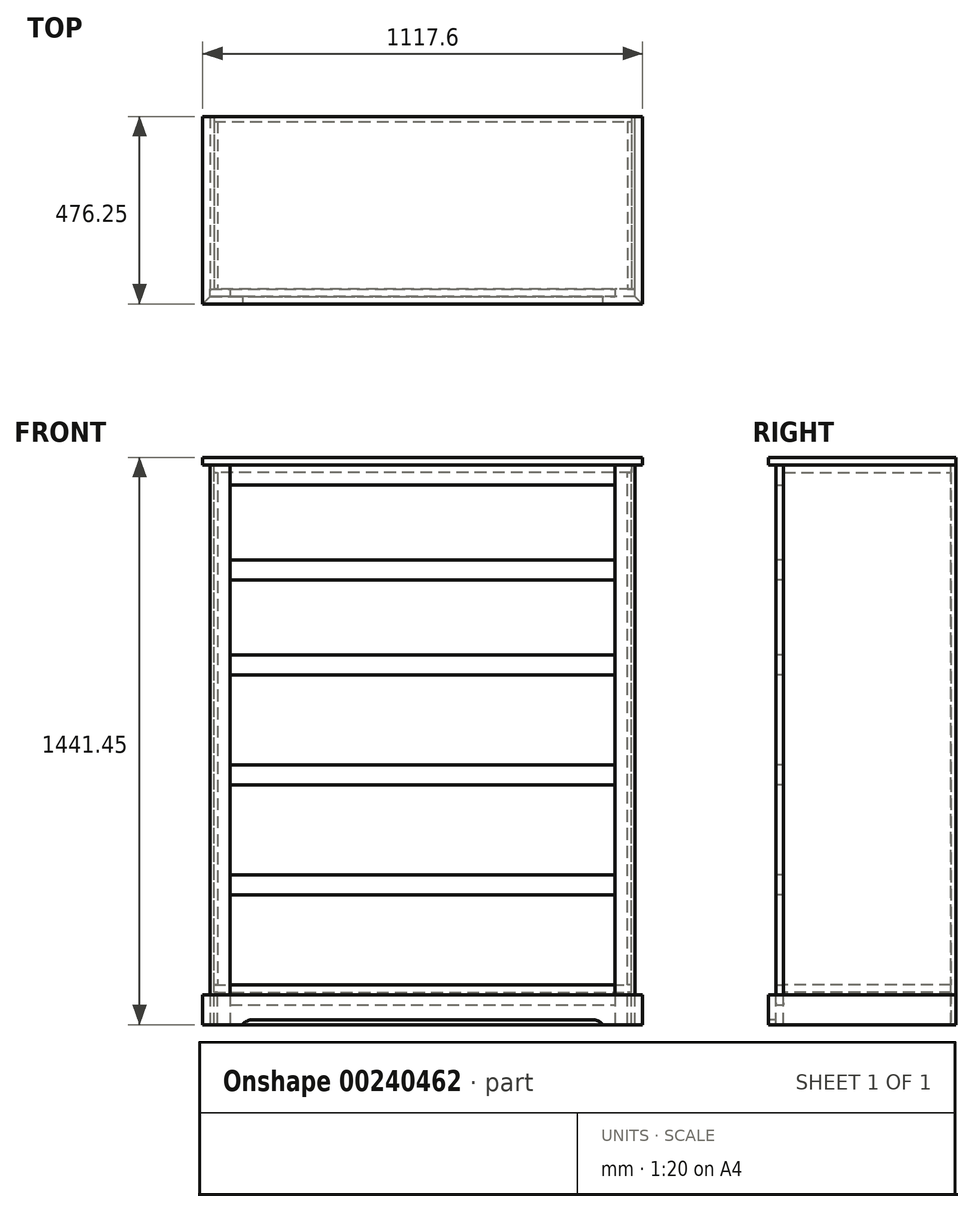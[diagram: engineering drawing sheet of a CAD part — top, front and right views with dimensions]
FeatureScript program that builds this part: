
annotation { "Feature Type Name" : "Feature", "Feature Type Description" : "" }
export const myFeature = defineFeature(function(context is Context, id is Id, definition is map)
    precondition{}
    {
        {
            var Q0;
            Q0=qCreatedBy(makeId("Right.planeOp"),FACE);
            var sketch = newSketch(context, id + "F0", { "sketchPlane" : qUnion([Q0])});
            skLineSegment(sketch, "E0.bottom", {"start": v(0, 0) * mm, "end": v(438.15, 0) * mm});
            skLineSegment(sketch, "E0.top", {"start": v(0, 1422.4) * mm, "end": v(438.15, 1422.4) * mm});
            skLineSegment(sketch, "E0.left", {"start": v(0, 0) * mm, "end": v(0, 1422.4) * mm});
            skLineSegment(sketch, "E0.right", {"start": v(438.15, 0) * mm, "end": v(438.15, 1422.4) * mm});
            skSolve(sketch);
        }
        {
            var Q0;
            Q0 = qSketchRegion(id + "F0", true);
            extrude(context, id + "F1", {"entities" : qUnion([Q0]), "oppositeDirection" : true, "depth" : 19.05 * mm});
        }
        {
            var Q0;
            Q0=makeQuery(id+"F1.opExtrude","SWEPT_FACE",FACE,{"disambiguationData":[OSD([sQuery(id+"F0.wireOp",EDGE,"E0.left")])]});
            var sketch = newSketch(context, id + "F2", { "sketchPlane" : qUnion([Q0])});
            skLineSegment(sketch, "E1.bottom", {"start": v(-9.52, 82.55) * mm, "end": v(-1069.98, 82.55) * mm});
            skLineSegment(sketch, "E1.top", {"start": v(-9.52, 101.6) * mm, "end": v(-1069.98, 101.6) * mm});
            skLineSegment(sketch, "E1.left", {"start": v(-9.52, 82.55) * mm, "end": v(-9.52, 101.6) * mm});
            skLineSegment(sketch, "E1.right", {"start": v(-1069.98, 82.55) * mm, "end": v(-1069.98, 101.6) * mm});
            skSolve(sketch);
        }
        {
            var Q0;
            Q0 = qSketchRegion(id + "F2", true);
            extrude(context, id + "F3", {"entities" : qUnion([Q0]), "oppositeDirection" : true, "depth" : 438.15 * mm});
        }
        {
            var Q0;
            Q0=makeQuery(id+"F3.opExtrude","SWEPT_BODY",BODY,{"disambiguationData":[OSD([sQuery(id+"F2.wireOp",EDGE,"E1.bottom"),sQuery(id+"F2.wireOp",EDGE,"E1.top"),sQuery(id+"F2.wireOp",EDGE,"E1.left"),sQuery(id+"F2.wireOp",EDGE,"E1.right")])]});
            var Q1;
            Q1=makeQuery(id+"F1.opExtrude","SWEPT_BODY",BODY,{"disambiguationData":[OSD([sQuery(id+"F0.wireOp",EDGE,"E0.bottom"),sQuery(id+"F0.wireOp",EDGE,"E0.top"),sQuery(id+"F0.wireOp",EDGE,"E0.left"),sQuery(id+"F0.wireOp",EDGE,"E0.right")])]});
            booleanBodies(context, id + "F4", {"operationType" : BooleanOperationType.SUBTRACTION, "tools" : qUnion([Q0]), "targets" : qUnion([Q1]), "keepTools" : true});
        }
        {
            var Q0;
            Q0=makeQuery(id+"F3.opExtrude","CAP_FACE",FACE,{"disambiguationData":[OSD([sQuery(id+"F2.wireOp",EDGE,"E1.bottom"),sQuery(id+"F2.wireOp",EDGE,"E1.top"),sQuery(id+"F2.wireOp",EDGE,"E1.left"),sQuery(id+"F2.wireOp",EDGE,"E1.right")])],"isStart":true});
            var sketch = newSketch(context, id + "F5", { "sketchPlane" : qUnion([Q0])});
            skLineSegment(sketch, "E2.bottom", {"start": v(-1079.5, 1422.4) * mm, "end": v(-1060.45, 1422.4) * mm});
            skLineSegment(sketch, "E2.top", {"start": v(-1079.5, 0) * mm, "end": v(-1060.45, 0) * mm});
            skLineSegment(sketch, "E2.left", {"start": v(-1079.5, 1422.4) * mm, "end": v(-1079.5, 0) * mm});
            skLineSegment(sketch, "E2.right", {"start": v(-1060.45, 1422.4) * mm, "end": v(-1060.45, 0) * mm});
            skSolve(sketch);
        }
        {
            var Q0;
            Q0 = qSketchRegion(id + "F5", true);
            extrude(context, id + "F6", {"entities" : qUnion([Q0]), "oppositeDirection" : true, "depth" : 438.15 * mm});
        }
        {
            var Q0;
            Q0=makeQuery(id+"F3.opExtrude","SWEPT_BODY",BODY,{"disambiguationData":[OSD([sQuery(id+"F2.wireOp",EDGE,"E1.bottom"),sQuery(id+"F2.wireOp",EDGE,"E1.top"),sQuery(id+"F2.wireOp",EDGE,"E1.left"),sQuery(id+"F2.wireOp",EDGE,"E1.right")])]});
            var Q1;
            Q1=makeQuery(id+"F6.opExtrude","SWEPT_BODY",BODY,{"disambiguationData":[OSD([sQuery(id+"F5.wireOp",EDGE,"E2.bottom"),sQuery(id+"F5.wireOp",EDGE,"E2.top"),sQuery(id+"F5.wireOp",EDGE,"E2.left"),sQuery(id+"F5.wireOp",EDGE,"E2.right")])]});
            booleanBodies(context, id + "F7", {"operationType" : BooleanOperationType.SUBTRACTION, "tools" : qUnion([Q0]), "targets" : qUnion([Q1]), "keepTools" : true});
        }
        {
            var Q0;
            Q0=makeQuery(id+"F6.opExtrude","CAP_FACE",FACE,{"disambiguationData":[OSD([sQuery(id+"F5.wireOp",EDGE,"E2.bottom"),sQuery(id+"F5.wireOp",EDGE,"E2.top"),sQuery(id+"F5.wireOp",EDGE,"E2.left"),sQuery(id+"F5.wireOp",EDGE,"E2.right")])],"isStart":true});
            var sketch = newSketch(context, id + "F8", { "sketchPlane" : qUnion([Q0])});
            skLineSegment(sketch, "E3.bottom", {"start": v(-1069.98, 1422.4) * mm, "end": v(-9.53, 1422.4) * mm});
            skLineSegment(sketch, "E3.top", {"start": v(-1069.98, 1403.35) * mm, "end": v(-9.53, 1403.35) * mm});
            skLineSegment(sketch, "E3.left", {"start": v(-1069.98, 1422.4) * mm, "end": v(-1069.98, 1403.35) * mm});
            skLineSegment(sketch, "E3.right", {"start": v(-9.53, 1422.4) * mm, "end": v(-9.53, 1403.35) * mm});
            skSolve(sketch);
        }
        {
            var Q0;
            Q0 = qSketchRegion(id + "F8", true);
            extrude(context, id + "F9", {"entities" : qUnion([Q0]), "oppositeDirection" : true, "depth" : 438.15 * mm});
        }
        {
            var Q0;
            Q0=makeQuery(id+"F9.opExtrude","SWEPT_BODY",BODY,{"disambiguationData":[OSD([sQuery(id+"F8.wireOp",EDGE,"E3.bottom"),sQuery(id+"F8.wireOp",EDGE,"E3.top"),sQuery(id+"F8.wireOp",EDGE,"E3.left"),sQuery(id+"F8.wireOp",EDGE,"E3.right")])]});
            var Q1;
            Q1=makeQuery(id+"F6.opExtrude","SWEPT_BODY",BODY,{"disambiguationData":[OSD([sQuery(id+"F5.wireOp",EDGE,"E2.bottom"),sQuery(id+"F5.wireOp",EDGE,"E2.top"),sQuery(id+"F5.wireOp",EDGE,"E2.left"),sQuery(id+"F5.wireOp",EDGE,"E2.right")])]});
            var Q2;
            Q2=makeQuery(id+"F1.opExtrude","SWEPT_BODY",BODY,{"disambiguationData":[OSD([sQuery(id+"F0.wireOp",EDGE,"E0.bottom"),sQuery(id+"F0.wireOp",EDGE,"E0.top"),sQuery(id+"F0.wireOp",EDGE,"E0.left"),sQuery(id+"F0.wireOp",EDGE,"E0.right")])]});
            booleanBodies(context, id + "F10", {"operationType" : BooleanOperationType.SUBTRACTION, "tools" : qUnion([Q0]), "targets" : qUnion([Q1, Q2]), "keepTools" : true});
        }
        {
            var Q0;
            Q0=makeQuery(id+"F9.opExtrude","SWEPT_FACE",FACE,{"disambiguationData":[OSD([sQuery(id+"F8.wireOp",EDGE,"E3.bottom")])]});
            var sketch = newSketch(context, id + "F11", { "sketchPlane" : qUnion([Q0])});
            skLineSegment(sketch, "E4.bottom", {"start": v(-1069.98, 438.15) * mm, "end": v(-9.53, 438.15) * mm});
            skLineSegment(sketch, "E4.top", {"start": v(-1069.98, 425.45) * mm, "end": v(-9.53, 425.45) * mm});
            skLineSegment(sketch, "E4.left", {"start": v(-1069.98, 438.15) * mm, "end": v(-1069.98, 425.45) * mm});
            skLineSegment(sketch, "E4.right", {"start": v(-9.53, 438.15) * mm, "end": v(-9.53, 425.45) * mm});
            skSolve(sketch);
        }
        {
            var Q0;
            Q0 = qSketchRegion(id + "F11", true);
            extrude(context, id + "F12", {"entities" : qUnion([Q0]), "oppositeDirection" : true, "depth" : 1422.4 * mm});
        }
        {
            var Q0;
            Q0=makeQuery(id+"F12.opExtrude","SWEPT_BODY",BODY,{"disambiguationData":[OSD([sQuery(id+"F11.wireOp",EDGE,"E4.bottom"),sQuery(id+"F11.wireOp",EDGE,"E4.top"),sQuery(id+"F11.wireOp",EDGE,"E4.left"),sQuery(id+"F11.wireOp",EDGE,"E4.right")])]});
            var Q1;
            Q1=makeQuery(id+"F6.opExtrude","SWEPT_BODY",BODY,{"disambiguationData":[OSD([sQuery(id+"F5.wireOp",EDGE,"E2.bottom"),sQuery(id+"F5.wireOp",EDGE,"E2.top"),sQuery(id+"F5.wireOp",EDGE,"E2.left"),sQuery(id+"F5.wireOp",EDGE,"E2.right")])]});
            var Q2;
            Q2=makeQuery(id+"F9.opExtrude","SWEPT_BODY",BODY,{"disambiguationData":[OSD([sQuery(id+"F8.wireOp",EDGE,"E3.bottom"),sQuery(id+"F8.wireOp",EDGE,"E3.top"),sQuery(id+"F8.wireOp",EDGE,"E3.left"),sQuery(id+"F8.wireOp",EDGE,"E3.right")])]});
            var Q3;
            Q3=makeQuery(id+"F1.opExtrude","SWEPT_BODY",BODY,{"disambiguationData":[OSD([sQuery(id+"F0.wireOp",EDGE,"E0.bottom"),sQuery(id+"F0.wireOp",EDGE,"E0.top"),sQuery(id+"F0.wireOp",EDGE,"E0.left"),sQuery(id+"F0.wireOp",EDGE,"E0.right")])]});
            var Q4;
            Q4=makeQuery(id+"F3.opExtrude","SWEPT_BODY",BODY,{"disambiguationData":[OSD([sQuery(id+"F2.wireOp",EDGE,"E1.bottom"),sQuery(id+"F2.wireOp",EDGE,"E1.top"),sQuery(id+"F2.wireOp",EDGE,"E1.left"),sQuery(id+"F2.wireOp",EDGE,"E1.right")])]});
            booleanBodies(context, id + "F13", {"operationType" : BooleanOperationType.SUBTRACTION, "tools" : qUnion([Q0]), "targets" : qUnion([Q1, Q2, Q3, Q4]), "keepTools" : true});
        }
        {
            var Q0;
            Q0=makeQuery(id+"F6.opExtrude","CAP_FACE",FACE,{"disambiguationData":[OSD([sQuery(id+"F5.wireOp",EDGE,"E2.bottom"),sQuery(id+"F5.wireOp",EDGE,"E2.top"),sQuery(id+"F5.wireOp",EDGE,"E2.left"),sQuery(id+"F5.wireOp",EDGE,"E2.right")])],"isStart":true});
            var sketch = newSketch(context, id + "F14", { "sketchPlane" : qUnion([Q0])});
            skLineSegment(sketch, "E5.bottom", {"start": v(-1079.5, 1422.4) * mm, "end": v(-1028.7, 1422.4) * mm});
            skLineSegment(sketch, "E5.top", {"start": v(-1079.5, 0) * mm, "end": v(-1028.7, 0) * mm});
            skLineSegment(sketch, "E5.left", {"start": v(-1079.5, 1422.4) * mm, "end": v(-1079.5, 0) * mm});
            skLineSegment(sketch, "E5.right", {"start": v(-1028.7, 1422.4) * mm, "end": v(-1028.7, 0) * mm});
            skSolve(sketch);
        }
        {
            var Q0;
            Q0 = qSketchRegion(id + "F14", true);
            extrude(context, id + "F15", {"entities" : qUnion([Q0]), "depth" : 19.05 * mm});
        }
        {
            var Q0;
            Q0=makeQuery(id+"F1.opExtrude","SWEPT_FACE",FACE,{"disambiguationData":[OSD([sQuery(id+"F0.wireOp",EDGE,"E0.left")])]});
            var sketch = newSketch(context, id + "F16", { "sketchPlane" : qUnion([Q0])});
            skLineSegment(sketch, "E6.bottom", {"start": v(0, 1422.4) * mm, "end": v(-50.8, 1422.4) * mm});
            skLineSegment(sketch, "E6.top", {"start": v(0, 0) * mm, "end": v(-50.8, 0) * mm});
            skLineSegment(sketch, "E6.left", {"start": v(0, 1422.4) * mm, "end": v(0, 0) * mm});
            skLineSegment(sketch, "E6.right", {"start": v(-50.8, 1422.4) * mm, "end": v(-50.8, 0) * mm});
            skSolve(sketch);
        }
        {
            var Q0;
            Q0 = qSketchRegion(id + "F16", true);
            extrude(context, id + "F17", {"entities" : qUnion([Q0]), "depth" : 19.05 * mm});
        }
        {
            var Q0;
            Q0=makeQuery(id+"F3.opExtrude","CAP_FACE",FACE,{"disambiguationData":[OSD([sQuery(id+"F2.wireOp",EDGE,"E1.bottom"),sQuery(id+"F2.wireOp",EDGE,"E1.top"),sQuery(id+"F2.wireOp",EDGE,"E1.left"),sQuery(id+"F2.wireOp",EDGE,"E1.right")])],"isStart":true});
            var sketch = newSketch(context, id + "F18", { "sketchPlane" : qUnion([Q0])});
            skLineSegment(sketch, "E7.bottom", {"start": v(-1028.7, 101.6) * mm, "end": v(-50.8, 101.6) * mm});
            skLineSegment(sketch, "E7.top", {"start": v(-1028.7, 50.8) * mm, "end": v(-50.8, 50.8) * mm});
            skLineSegment(sketch, "E7.left", {"start": v(-1028.7, 101.6) * mm, "end": v(-1028.7, 50.8) * mm});
            skLineSegment(sketch, "E7.right", {"start": v(-50.8, 101.6) * mm, "end": v(-50.8, 50.8) * mm});
            skSolve(sketch);
        }
        {
            var Q0;
            Q0 = qSketchRegion(id + "F18", true);
            extrude(context, id + "F19", {"entities" : qUnion([Q0]), "depth" : 19.05 * mm});
        }
        {
            var Q0;
            Q0=makeQuery(id+"F9.opExtrude","CAP_FACE",FACE,{"disambiguationData":[OSD([sQuery(id+"F8.wireOp",EDGE,"E3.bottom"),sQuery(id+"F8.wireOp",EDGE,"E3.top"),sQuery(id+"F8.wireOp",EDGE,"E3.left"),sQuery(id+"F8.wireOp",EDGE,"E3.right")])],"isStart":true});
            var sketch = newSketch(context, id + "F20", { "sketchPlane" : qUnion([Q0])});
            skLineSegment(sketch, "E8.bottom", {"start": v(-1028.7, 1422.4) * mm, "end": v(-50.8, 1422.4) * mm});
            skLineSegment(sketch, "E8.top", {"start": v(-1028.7, 1371.6) * mm, "end": v(-50.8, 1371.6) * mm});
            skLineSegment(sketch, "E8.left", {"start": v(-1028.7, 1422.4) * mm, "end": v(-1028.7, 1371.6) * mm});
            skLineSegment(sketch, "E8.right", {"start": v(-50.8, 1422.4) * mm, "end": v(-50.8, 1371.6) * mm});
            skSolve(sketch);
        }
        {
            var Q0;
            Q0 = qSketchRegion(id + "F20", true);
            extrude(context, id + "F21", {"entities" : qUnion([Q0]), "depth" : 19.05 * mm});
        }
        {
            var Q0;
            Q0=makeQuery(id+"F15.opExtrude","CAP_FACE",FACE,{"disambiguationData":[OSD([sQuery(id+"F14.wireOp",EDGE,"E5.bottom"),sQuery(id+"F14.wireOp",EDGE,"E5.top"),sQuery(id+"F14.wireOp",EDGE,"E5.left"),sQuery(id+"F14.wireOp",EDGE,"E5.right")])],"isStart":false});
            var sketch = newSketch(context, id + "F22", { "sketchPlane" : qUnion([Q0])});
            skLineSegment(sketch, "E9.bottom", {"start": v(-1028.7, 381) * mm, "end": v(-50.8, 381) * mm});
            skLineSegment(sketch, "E9.top", {"start": v(-1028.7, 330.2) * mm, "end": v(-50.8, 330.2) * mm});
            skLineSegment(sketch, "E9.left", {"start": v(-1028.7, 381) * mm, "end": v(-1028.7, 330.2) * mm});
            skLineSegment(sketch, "E9.right", {"start": v(-50.8, 381) * mm, "end": v(-50.8, 330.2) * mm});
            skSolve(sketch);
        }
        {
            var Q0;
            Q0 = qSketchRegion(id + "F22", true);
            extrude(context, id + "F23", {"entities" : qUnion([Q0]), "oppositeDirection" : true, "depth" : 19.05 * mm});
        }
        {
            var Q0;
            Q0=makeQuery(id+"F15.opExtrude","CAP_FACE",FACE,{"disambiguationData":[OSD([sQuery(id+"F14.wireOp",EDGE,"E5.bottom"),sQuery(id+"F14.wireOp",EDGE,"E5.top"),sQuery(id+"F14.wireOp",EDGE,"E5.left"),sQuery(id+"F14.wireOp",EDGE,"E5.right")])],"isStart":false});
            var sketch = newSketch(context, id + "F24", { "sketchPlane" : qUnion([Q0])});
            skLineSegment(sketch, "E10.bottom", {"start": v(-1028.7, 660.4) * mm, "end": v(-50.8, 660.4) * mm});
            skLineSegment(sketch, "E10.top", {"start": v(-1028.7, 609.6) * mm, "end": v(-50.8, 609.6) * mm});
            skLineSegment(sketch, "E10.left", {"start": v(-1028.7, 660.4) * mm, "end": v(-1028.7, 609.6) * mm});
            skLineSegment(sketch, "E10.right", {"start": v(-50.8, 660.4) * mm, "end": v(-50.8, 609.6) * mm});
            skSolve(sketch);
        }
        {
            var Q0;
            Q0 = qSketchRegion(id + "F24", true);
            extrude(context, id + "F25", {"entities" : qUnion([Q0]), "oppositeDirection" : true, "depth" : 19.05 * mm});
        }
        {
            var Q0;
            Q0=makeQuery(id+"F15.opExtrude","CAP_FACE",FACE,{"disambiguationData":[OSD([sQuery(id+"F14.wireOp",EDGE,"E5.bottom"),sQuery(id+"F14.wireOp",EDGE,"E5.top"),sQuery(id+"F14.wireOp",EDGE,"E5.left"),sQuery(id+"F14.wireOp",EDGE,"E5.right")])],"isStart":false});
            var sketch = newSketch(context, id + "F26", { "sketchPlane" : qUnion([Q0])});
            skLineSegment(sketch, "E11.bottom", {"start": v(-1028.7, 939.8) * mm, "end": v(-50.8, 939.8) * mm});
            skLineSegment(sketch, "E11.top", {"start": v(-1028.7, 889) * mm, "end": v(-50.8, 889) * mm});
            skLineSegment(sketch, "E11.left", {"start": v(-1028.7, 939.8) * mm, "end": v(-1028.7, 889) * mm});
            skLineSegment(sketch, "E11.right", {"start": v(-50.8, 939.8) * mm, "end": v(-50.8, 889) * mm});
            skSolve(sketch);
        }
        {
            var Q0;
            Q0 = qSketchRegion(id + "F26", true);
            extrude(context, id + "F27", {"entities" : qUnion([Q0]), "oppositeDirection" : true, "depth" : 19.05 * mm});
        }
        {
            var Q0;
            Q0=makeQuery(id+"F15.opExtrude","CAP_FACE",FACE,{"disambiguationData":[OSD([sQuery(id+"F14.wireOp",EDGE,"E5.bottom"),sQuery(id+"F14.wireOp",EDGE,"E5.top"),sQuery(id+"F14.wireOp",EDGE,"E5.left"),sQuery(id+"F14.wireOp",EDGE,"E5.right")])],"isStart":false});
            var sketch = newSketch(context, id + "F28", { "sketchPlane" : qUnion([Q0])});
            skLineSegment(sketch, "E12.bottom", {"start": v(-1028.7, 1181.1) * mm, "end": v(-50.8, 1181.1) * mm});
            skLineSegment(sketch, "E12.top", {"start": v(-1028.7, 1130.3) * mm, "end": v(-50.8, 1130.3) * mm});
            skLineSegment(sketch, "E12.left", {"start": v(-1028.7, 1181.1) * mm, "end": v(-1028.7, 1130.3) * mm});
            skLineSegment(sketch, "E12.right", {"start": v(-50.8, 1181.1) * mm, "end": v(-50.8, 1130.3) * mm});
            skSolve(sketch);
        }
        {
            var Q0;
            Q0 = qSketchRegion(id + "F28", true);
            extrude(context, id + "F29", {"entities" : qUnion([Q0]), "oppositeDirection" : true, "depth" : 19.05 * mm});
        }
        {
            var Q0;
            Q0=makeQuery(id+"F9.opExtrude","SWEPT_FACE",FACE,{"disambiguationData":[OSD([sQuery(id+"F8.wireOp",EDGE,"E3.bottom")])]});
            var sketch = newSketch(context, id + "F30", { "sketchPlane" : qUnion([Q0])});
            skLineSegment(sketch, "E13.bottom", {"start": v(-1098.55, 438.15) * mm, "end": v(19.05, 438.15) * mm});
            skLineSegment(sketch, "E13.top", {"start": v(-1098.55, -38.1) * mm, "end": v(19.05, -38.1) * mm});
            skLineSegment(sketch, "E13.left", {"start": v(-1098.55, 438.15) * mm, "end": v(-1098.55, -38.1) * mm});
            skLineSegment(sketch, "E13.right", {"start": v(19.05, 438.15) * mm, "end": v(19.05, -38.1) * mm});
            skSolve(sketch);
        }
        {
            var Q0;
            Q0 = qSketchRegion(id + "F30", true);
            extrude(context, id + "F31", {"entities" : qUnion([Q0]), "depth" : 19.05 * mm});
        }
        {
            var Q0;
            Q0=makeQuery(id+"F6.opExtrude","SWEPT_FACE",FACE,{"disambiguationData":[OSD([sQuery(id+"F5.wireOp",EDGE,"E2.top")])]});
            var sketch = newSketch(context, id + "F32", { "sketchPlane" : qUnion([Q0])});
            skLineSegment(sketch, "E14.bottom", {"start": v(-1079.5, -438.15) * mm, "end": v(-1098.55, -438.15) * mm});
            skLineSegment(sketch, "E14.left", {"start": v(-1079.5, -438.15) * mm, "end": v(-1079.5, 19.05) * mm});
            skLineSegment(sketch, "E14.right", {"start": v(-1098.55, -438.15) * mm, "end": v(-1098.55, 38.1) * mm});
            skLineSegment(sketch, "E15", {"start": v(-1098.55, 38.1) * mm, "end": v(-1079.5, 19.05) * mm});
            skSolve(sketch);
        }
        {
            var Q0;
            Q0 = qSketchRegion(id + "F32", true);
            extrude(context, id + "F33", {"entities" : qUnion([Q0]), "oppositeDirection" : true, "depth" : 76.2 * mm});
        }
        {
            var Q0;
            Q0=makeQuery(id+"F1.opExtrude","SWEPT_FACE",FACE,{"disambiguationData":[OSD([sQuery(id+"F0.wireOp",EDGE,"E0.bottom")])]});
            var sketch = newSketch(context, id + "F34", { "sketchPlane" : qUnion([Q0])});
            skLineSegment(sketch, "E16.bottom", {"start": v(0, -438.15) * mm, "end": v(19.05, -438.15) * mm});
            skLineSegment(sketch, "E16.left", {"start": v(0, -438.15) * mm, "end": v(0, 19.05) * mm});
            skLineSegment(sketch, "E16.right", {"start": v(19.05, -438.15) * mm, "end": v(19.05, 38.1) * mm});
            skLineSegment(sketch, "E17", {"start": v(19.05, 38.1) * mm, "end": v(0, 19.05) * mm});
            skSolve(sketch);
        }
        {
            var Q0;
            Q0 = qSketchRegion(id + "F34", true);
            extrude(context, id + "F35", {"entities" : qUnion([Q0]), "oppositeDirection" : true, "depth" : 76.2 * mm});
        }
        {
            var Q0;
            Q0=makeQuery(id+"F17.opExtrude","SWEPT_FACE",FACE,{"disambiguationData":[OSD([sQuery(id+"F16.wireOp",EDGE,"E6.top")])]});
            var sketch = newSketch(context, id + "F36", { "sketchPlane" : qUnion([Q0])});
            skLineSegment(sketch, "E18", {"start": v(0, 19.05) * mm, "end": v(19.05, 38.1) * mm});
            skLineSegment(sketch, "E19", {"start": v(19.05, 38.1) * mm, "end": v(-1098.55, 38.1) * mm});
            skLineSegment(sketch, "E20", {"start": v(-1098.55, 38.1) * mm, "end": v(-1079.5, 19.05) * mm});
            skLineSegment(sketch, "E21", {"start": v(-1079.5, 19.05) * mm, "end": v(0, 19.05) * mm});
            skSolve(sketch);
        }
        {
            var Q0;
            Q0 = qSketchRegion(id + "F36", true);
            extrude(context, id + "F37", {"entities" : qUnion([Q0]), "oppositeDirection" : true, "depth" : 76.2 * mm});
        }
        {
            var Q0;
            Q0=makeQuery(id+"F37.opExtrude","SWEPT_FACE",FACE,{"disambiguationData":[OSD([sQuery(id+"F36.wireOp",EDGE,"E19")])]});
            var sketch = newSketch(context, id + "F38", { "sketchPlane" : qUnion([Q0])});
            skLineSegment(sketch, "E22", {"start": v(-971.55, 12.7) * mm, "end": v(-107.95, 12.7) * mm});
            skArc(sketch, "E23", {"start": v(-971.55, 12.7) * mm, "mid": v(-985.75, 9.35) * mm, "end": v(-996.95, 0) * mm});
            skArc(sketch, "E24", {"start": v(-82.55, 0) * mm, "mid": v(-93.75, 9.35) * mm, "end": v(-107.95, 12.7) * mm});
            skLineSegment(sketch, "E25", {"start": v(-996.95, 0) * mm, "end": v(-82.55, 0) * mm});
            skSolve(sketch);
        }
        {
            var Q0;
            Q0 = qSketchRegion(id + "F38", true);
            extrude(context, id + "F39", {"entities" : qUnion([Q0]), "operationType" : NewBodyOperationType.REMOVE, "oppositeDirection" : true, "depth" : 19.05 * mm});
        }
    });
